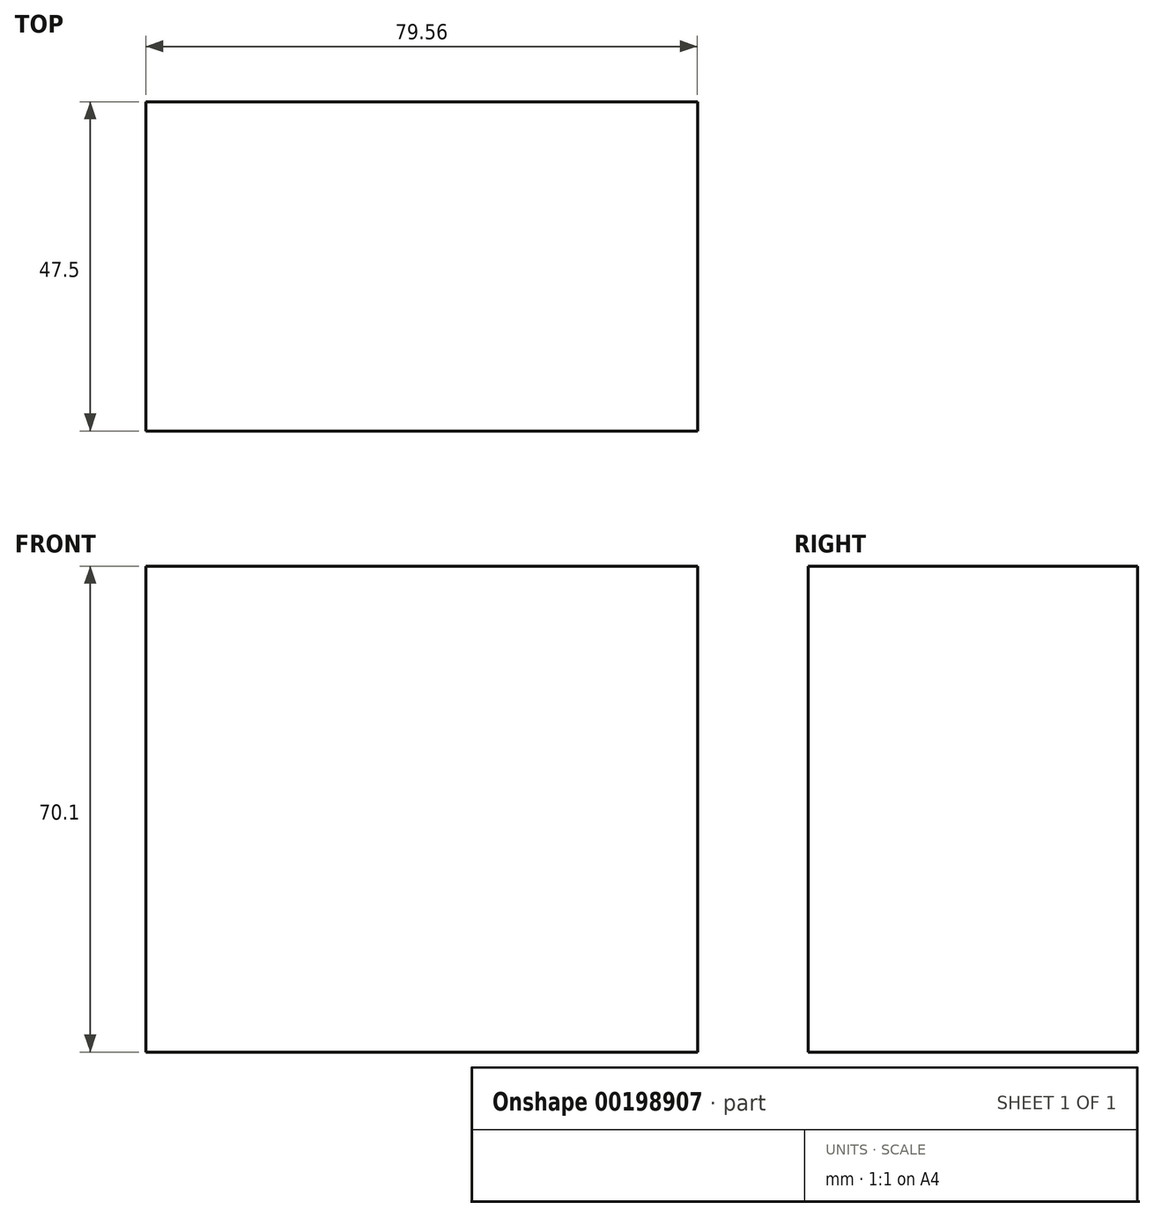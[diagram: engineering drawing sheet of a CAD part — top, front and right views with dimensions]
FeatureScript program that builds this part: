
annotation { "Feature Type Name" : "Feature", "Feature Type Description" : "" }
export const myFeature = defineFeature(function(context is Context, id is Id, definition is map)
    precondition{}
    {
        {
            var Q0;
            Q0=qCreatedBy(makeId("Front.planeOp"),FACE);
            var sketch = newSketch(context, id + "F0", { "sketchPlane" : qUnion([Q0])});
            skLineSegment(sketch, "E0.bottom", {"start": v(39.78, -35.05) * mm, "end": v(-39.78, -35.05) * mm});
            skLineSegment(sketch, "E0.top", {"start": v(39.78, 35.05) * mm, "end": v(-39.78, 35.05) * mm});
            skLineSegment(sketch, "E0.left", {"start": v(39.78, -35.05) * mm, "end": v(39.78, 35.05) * mm});
            skLineSegment(sketch, "E0.right", {"start": v(-39.78, -35.05) * mm, "end": v(-39.78, 35.05) * mm});
            skPoint(sketch, "E0.middle", {"position": v(0, 0) * mm});
            skSolve(sketch);
        }
        {
            var Q0;
            Q0=makeQuery(id+"F0.imprint","IMPRINT",FACE,{"disambiguationData":[TD([[makeQuery(id+"F0.imprint","IMPRINT",EDGE,{"derivedFrom":sQuery(id+"F0.wireOp",EDGE,"E0.bottom")}),-1.0]])]});
            extrude(context, id + "F1", {"entities" : qUnion([Q0]), "depth" : 47.5 * mm});
        }
    });
